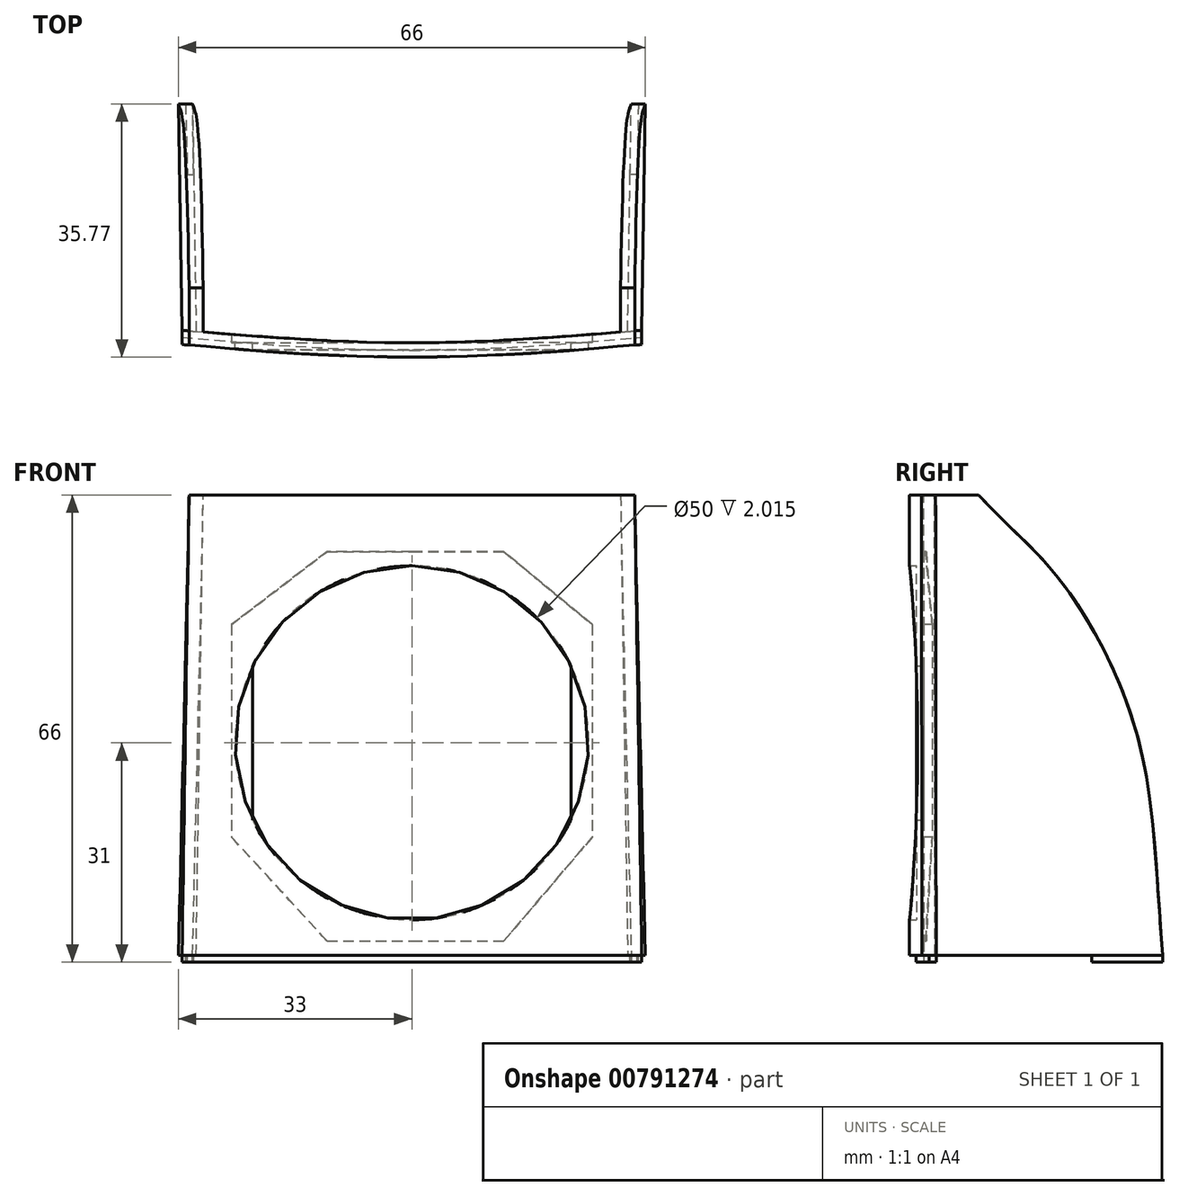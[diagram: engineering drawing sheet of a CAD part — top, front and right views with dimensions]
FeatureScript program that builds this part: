
annotation { "Feature Type Name" : "Feature", "Feature Type Description" : "" }
export const myFeature = defineFeature(function(context is Context, id is Id, definition is map)
    precondition{}
    {
        {
            var Q0;
            Q0=qCreatedBy(makeId("Front.planeOp"),FACE);
            var sketch = newSketch(context, id + "F0", { "sketchPlane" : qUnion([Q0])});
            skLineSegment(sketch, "E0", {"start": v(-32.5, -32.5) * mm, "end": v(32.5, -32.5) * mm});
            skLineSegment(sketch, "E1", {"start": v(32.5, -32.5) * mm, "end": v(31.5, 32.5) * mm});
            skLineSegment(sketch, "E2", {"start": v(31.5, 32.5) * mm, "end": v(-31.5, 32.5) * mm});
            skLineSegment(sketch, "E3", {"start": v(-31.5, 32.5) * mm, "end": v(-32.5, -32.5) * mm});
            skPoint(sketch, "E4", {"position": v(0, -32.5) * mm});
            skPoint(sketch, "E5", {"position": v(0, 32.5) * mm});
            skPoint(sketch, "E6", {"position": v(0, 0) * mm});
            skSolve(sketch);
        }
        {
            var Q0;
            Q0=makeQuery(id+"F0.imprint","IMPRINT",FACE,{"disambiguationData":[TD([[makeQuery(id+"F0.imprint","IMPRINT",EDGE,{"derivedFrom":sQuery(id+"F0.wireOp",EDGE,"E0")}),1.0]])]});
            extrude(context, id + "F1", {"entities" : qUnion([Q0]), "depth" : 5 * mm, "offsetDistance" : 25 * mm});
        }
        {
            var Q0;
            Q0=makeQuery(id+"F1.opExtrude","SWEPT_FACE",FACE,{"disambiguationData":[OSD([sQuery(id+"F0.wireOp",EDGE,"E0")])]});
            var sketch = newSketch(context, id + "F2", { "sketchPlane" : qUnion([Q0])});
            skFitSpline(sketch, "E7", {"points": [v(-32.5, 0) * mm, v(0, 1.76) * mm, v(32.5, 0) * mm], "startDerivative": vector(66, 5.28) * mm, "endDerivative": vector(66, -5.28) * mm});
            skLineSegment(sketch, "E8", {"start": v(-32.5, 0) * mm, "end": v(32.5, 0) * mm});
            skFitSpline(sketch, "E9.0", {"points": [v(-32.66, 2) * mm, v(-27.16, 2.43) * mm, v(-18.99, 3.1) * mm, v(-9.5, 3.58) * mm, v(-4.07, 3.73) * mm, v(0, 3.77) * mm, v(4.07, 3.73) * mm, v(9.5, 3.58) * mm, v(18.99, 3.1) * mm, v(27.16, 2.43) * mm, v(32.66, 2) * mm]});
            skLineSegment(sketch, "E10", {"start": v(32.66, 2) * mm, "end": v(32.5, 5) * mm});
            skLineSegment(sketch, "E11", {"start": v(32.5, 5) * mm, "end": v(-32.5, 5) * mm});
            skLineSegment(sketch, "E12", {"start": v(-32.5, 5) * mm, "end": v(-32.66, 2) * mm});
            skFitSpline(sketch, "E13.0", {"points": [v(-32.58, 1) * mm, v(-27.08, 1.44) * mm, v(-18.91, 2.1) * mm, v(-8.1, 2.65) * mm, v(0, 2.82) * mm, v(8.1, 2.65) * mm, v(18.91, 2.1) * mm, v(27.08, 1.44) * mm, v(32.58, 1) * mm]});
            skLineSegment(sketch, "E14", {"start": v(32.5, 0) * mm, "end": v(32.58, 1) * mm});
            skLineSegment(sketch, "E15", {"start": v(-32.5, 0) * mm, "end": v(-32.58, 1) * mm});
            skSolve(sketch);
        }
        {
            var Q0;
            {var subQ6=sQuery(id+"F2.wireOp",EDGE,"E11");Q0=makeQuery(id+"F2.imprint","IMPRINT",FACE,{"disambiguationData":[TD([[makeQuery(id+"F2.imprint","IMPRINT",EDGE,{"derivedFrom":subQ6}),-1.0]])]});}
            var Q1;
            Q1=makeQuery(id+"F2.imprint","IMPRINT",FACE,{"disambiguationData":[TD([[makeQuery(id+"F2.imprint","IMPRINT",EDGE,{"derivedFrom":sQuery(id+"F2.wireOp",EDGE,"E7")}),-1.0]])]});
            extrude(context, id + "F3", {"entities" : qUnion([Q0, Q1]), "operationType" : NewBodyOperationType.REMOVE, "oppositeDirection" : true, "depth" : 65 * mm, "offsetDistance" : 25 * mm});
        }
        {
            var Q0;
            Q0=qCreatedBy(makeId("Front.planeOp"),FACE);
            var sketch = newSketch(context, id + "F4", { "sketchPlane" : qUnion([Q0])});
            skCircle(sketch, "E16", {"center": v(0, -2.5) * mm, "radius": 25 * mm});
            skPoint(sketch, "E17", {"position": v(0, 22.5) * mm});
            skSolve(sketch);
        }
        {
            var Q0;
            Q0 = qSketchRegion(id + "F4", true);
            extrude(context, id + "F5", {"entities" : qUnion([Q0]), "operationType" : NewBodyOperationType.REMOVE, "depth" : 25 * mm, "offsetDistance" : 25 * mm});
        }
        {
            var Q0;
            Q0=makeQuery(id+"F1.opExtrude","SWEPT_FACE",FACE,{"disambiguationData":[OSD([sQuery(id+"F0.wireOp",EDGE,"E0")])]});
            var sketch = newSketch(context, id + "F6", { "sketchPlane" : qUnion([Q0])});
            skLineSegment(sketch, "E18", {"start": v(-32.5, 0) * mm, "end": v(-33, -32) * mm});
            skLineSegment(sketch, "E19", {"start": v(-33, -32) * mm, "end": v(-31, -32) * mm});
            skLineSegment(sketch, "E20", {"start": v(-31, -32) * mm, "end": v(-30.5, 0.16) * mm});
            skLineSegment(sketch, "E21", {"start": v(-30.5, 0.16) * mm, "end": v(-32.5, 0) * mm});
            skLineSegment(sketch, "E22", {"start": v(32.5, 0) * mm, "end": v(30.5, 0.16) * mm});
            skLineSegment(sketch, "E23", {"start": v(30.5, 0.16) * mm, "end": v(31, -32) * mm});
            skLineSegment(sketch, "E24", {"start": v(31, -32) * mm, "end": v(33, -32) * mm});
            skLineSegment(sketch, "E25", {"start": v(33, -32) * mm, "end": v(32.5, 0) * mm});
            skPoint(sketch, "E26", {"position": v(0, -32) * mm});
            skLineSegment(sketch, "E27", {"start": v(32.5, 0) * mm, "end": v(30.5, 0) * mm, "construction": true});
            skLineSegment(sketch, "E28", {"start": v(-32.5, 0) * mm, "end": v(-30.5, 0) * mm, "construction": true});
            skSolve(sketch);
        }
        {
            var Q0;
            Q0=makeQuery(id+"F1.opExtrude","SWEPT_FACE",FACE,{"disambiguationData":[OSD([sQuery(id+"F0.wireOp",EDGE,"E2")])]});
            var sketch = newSketch(context, id + "F7", { "sketchPlane" : qUnion([Q0])});
            skLineSegment(sketch, "E29", {"start": v(-31.5, -0.08) * mm, "end": v(-29.5, -0.24) * mm});
            skLineSegment(sketch, "E30", {"start": v(-29.5, -0.24) * mm, "end": v(-29.5, 32) * mm});
            skLineSegment(sketch, "E31", {"start": v(-29.5, 32) * mm, "end": v(-31.5, 32) * mm});
            skLineSegment(sketch, "E32", {"start": v(-31.5, 32) * mm, "end": v(-31.5, -0.08) * mm});
            skLineSegment(sketch, "E33", {"start": v(31.5, -0.08) * mm, "end": v(29.5, -0.24) * mm});
            skLineSegment(sketch, "E34", {"start": v(29.5, -0.24) * mm, "end": v(29.5, 32) * mm});
            skLineSegment(sketch, "E35", {"start": v(29.5, 32) * mm, "end": v(31.5, 32) * mm});
            skLineSegment(sketch, "E36", {"start": v(31.5, 32) * mm, "end": v(31.5, -0.08) * mm});
            skLineSegment(sketch, "E37", {"start": v(-31.5, -0.08) * mm, "end": v(-29.5, -0.08) * mm, "construction": true});
            skLineSegment(sketch, "E38", {"start": v(31.5, -0.08) * mm, "end": v(29.5, -0.08) * mm, "construction": true});
            skPoint(sketch, "E39", {"position": v(0, 32) * mm});
            skSolve(sketch);
        }
        {
            var Q1;
            Q1=makeQuery(id+"F6.imprint","IMPRINT",FACE,{"disambiguationData":[TD([[makeQuery(id+"F6.imprint","IMPRINT",EDGE,{"derivedFrom":sQuery(id+"F6.wireOp",EDGE,"E18")}),1.0]])]});
            var Q2;
            Q2=makeQuery(id+"F7.imprint","IMPRINT",FACE,{"disambiguationData":[TD([[makeQuery(id+"F7.imprint","IMPRINT",EDGE,{"derivedFrom":sQuery(id+"F7.wireOp",EDGE,"E29")}),1.0]])]});
            loft(context, id + "F8", {"operationType" : NewBodyOperationType.ADD, "sheetProfilesArray" : [{ "sheetProfileEntities" : qUnion([Q1]) }, { "sheetProfileEntities" : qUnion([Q2]) }]});
        }
        {
            var Q1;
            Q1=makeQuery(id+"F7.imprint","IMPRINT",FACE,{"disambiguationData":[TD([[makeQuery(id+"F7.imprint","IMPRINT",EDGE,{"derivedFrom":sQuery(id+"F7.wireOp",EDGE,"E33")}),1.0]])]});
            var Q2;
            Q2=makeQuery(id+"F6.imprint","IMPRINT",FACE,{"disambiguationData":[TD([[makeQuery(id+"F6.imprint","IMPRINT",EDGE,{"derivedFrom":sQuery(id+"F6.wireOp",EDGE,"E22")}),-1.0]])]});
            loft(context, id + "F9", {"operationType" : NewBodyOperationType.ADD, "sheetProfilesArray" : [{ "sheetProfileEntities" : qUnion([Q1]) }, { "sheetProfileEntities" : qUnion([Q2]) }]});
        }
        {
            var Q0;
            Q0=qCreatedBy(makeId("Right.planeOp"),FACE);
            var sketch = newSketch(context, id + "F10", { "sketchPlane" : qUnion([Q0])});
            skLineSegment(sketch, "E40", {"start": v(0, 32.5) * mm, "end": v(6, 32.5) * mm});
            skLineSegment(sketch, "E41", {"start": v(32, -32.5) * mm, "end": v(0, -32.5) * mm});
            skLineSegment(sketch, "E42", {"start": v(0, -32.5) * mm, "end": v(0, 32.5) * mm});
            skLineSegment(sketch, "E43", {"start": v(32, -32.5) * mm, "end": v(32, 32.5) * mm});
            skPoint(sketch, "E43.endSnap0", {"position": v(3, 32.5) * mm});
            skLineSegment(sketch, "E44", {"start": v(32, 32.5) * mm, "end": v(6, 32.5) * mm});
            skPoint(sketch, "E45", {"position": v(28, 0) * mm});
            skFitSpline(sketch, "E46", {"points": [v(6, 32.5) * mm, v(17, 21.1) * mm, v(28, 0) * mm, v(31, -18.45) * mm, v(32, -32.5) * mm], "startDerivative": vector(39.95, -44.58) * mm, "endDerivative": vector(5.9, -79.66) * mm});
            skSolve(sketch);
        }
        {
            var Q0;
            Q0=makeQuery(id+"F10.imprint","IMPRINT",FACE,{"disambiguationData":[TD([[makeQuery(id+"F10.imprint","IMPRINT",EDGE,{"derivedFrom":sQuery(id+"F10.wireOp",EDGE,"E43")}),1.0]])]});
            extrude(context, id + "F11", {"entities" : qUnion([Q0]), "operationType" : NewBodyOperationType.REMOVE, "endBound" : BoundingType.SYMMETRIC, "depth" : 70 * mm, "offsetDistance" : 25 * mm});
        }
        {
            var Q0;
            {var subQ0=sQuery(id+"F2.wireOp",EDGE,"E7");Q0=makeQuery(id+"F2.imprint","IMPRINT",FACE,{"disambiguationData":[TD([[makeQuery(id+"F2.imprint","IMPRINT",EDGE,{"derivedFrom":subQ0}),1.0]])]});}
            extrude(context, id + "F12", {"entities" : qUnion([Q0]), "operationType" : NewBodyOperationType.ADD, "depth" : 1 * mm, "offsetDistance" : 25 * mm});
        }
        {
            var Q0;
            Q0=makeQuery(id+"F6.imprint","IMPRINT",FACE,{"disambiguationData":[TD([[makeQuery(id+"F6.imprint","IMPRINT",EDGE,{"derivedFrom":sQuery(id+"F6.wireOp",EDGE,"E22")}),-1.0]])]});
            var sketch = newSketch(context, id + "F13", { "sketchPlane" : qUnion([Q0])});
            skLineSegment(sketch, "E47", {"start": v(31, -32) * mm, "end": v(32, -32) * mm});
            skLineSegment(sketch, "E48", {"start": v(32, -32) * mm, "end": v(31.85, -22) * mm});
            skLineSegment(sketch, "E49", {"start": v(31.85, -22) * mm, "end": v(30.85, -22) * mm});
            skLineSegment(sketch, "E50", {"start": v(30.85, -22) * mm, "end": v(31, -32) * mm});
            skLineSegment(sketch, "E51", {"start": v(-31, -32) * mm, "end": v(-32, -32) * mm});
            skLineSegment(sketch, "E52", {"start": v(-32, -32) * mm, "end": v(-31.73, -22) * mm});
            skLineSegment(sketch, "E53", {"start": v(-31.73, -22) * mm, "end": v(-30.85, -22) * mm});
            skLineSegment(sketch, "E54", {"start": v(-30.85, -22) * mm, "end": v(-31, -32) * mm});
            skSolve(sketch);
        }
        {
            var Q0;
            Q0 = qSketchRegion(id + "F13", true);
            extrude(context, id + "F14", {"entities" : qUnion([Q0]), "operationType" : NewBodyOperationType.ADD, "depth" : 1 * mm, "offsetDistance" : 25 * mm});
        }
        {
            var Q0;
            {var subQ1=sQuery(id+"F6.wireOp",EDGE,"E21");Q0=makeQuery(id+"F6.imprint","IMPRINT",FACE,{"disambiguationData":[TD([[makeQuery(id+"F6.imprint","IMPRINT",EDGE,{"derivedFrom":subQ1}),1.0]])]});}
            var sketch = newSketch(context, id + "F15", { "sketchPlane" : qUnion([Q0])});
            skLineSegment(sketch, "E55.bottom", {"start": v(-22.5, 1.76) * mm, "end": v(22.5, 1.76) * mm});
            skLineSegment(sketch, "E55.top", {"start": v(-22.5, 2.76) * mm, "end": v(22.5, 2.76) * mm});
            skLineSegment(sketch, "E55.left", {"start": v(-22.5, 1.76) * mm, "end": v(-22.5, 2.76) * mm});
            skLineSegment(sketch, "E55.right", {"start": v(22.5, 1.76) * mm, "end": v(22.5, 2.76) * mm});
            skPoint(sketch, "E55.middle", {"position": v(0, 2.26) * mm});
            skSolve(sketch);
        }
        {
            var Q0;
            Q0 = qSketchRegion(id + "F15", true);
            extrude(context, id + "F16", {"entities" : qUnion([Q0]), "operationType" : NewBodyOperationType.ADD, "oppositeDirection" : true, "depth" : 57.3 * mm, "offsetDistance" : 25 * mm});
        }
        {
            var Q0;
            Q0=makeQuery(id+"F16.opExtrude","SWEPT_FACE",FACE,{"disambiguationData":[OSD([sQuery(id+"F15.wireOp",EDGE,"E55.bottom")])]});
            var sketch = newSketch(context, id + "F17", { "sketchPlane" : qUnion([Q0])});
            skLineSegment(sketch, "E56", {"start": v(-13, 24.5) * mm, "end": v(12, 24.5) * mm});
            skLineSegment(sketch, "E57", {"start": v(12, 24.5) * mm, "end": v(25.5, 14.18) * mm});
            skLineSegment(sketch, "E58", {"start": v(25.5, 14.18) * mm, "end": v(25.5, -15.82) * mm});
            skLineSegment(sketch, "E59", {"start": v(25.5, -15.82) * mm, "end": v(12, -30.5) * mm});
            skLineSegment(sketch, "E60", {"start": v(12, -30.5) * mm, "end": v(-13, -30.5) * mm});
            skLineSegment(sketch, "E61", {"start": v(-13, -30.5) * mm, "end": v(-25.5, -15.82) * mm});
            skLineSegment(sketch, "E62", {"start": v(-25.5, -15.82) * mm, "end": v(-25.5, 14.18) * mm});
            skLineSegment(sketch, "E63", {"start": v(-25.5, 14.18) * mm, "end": v(-13, 24.5) * mm});
            skPoint(sketch, "E64", {"position": v(25.5, -0.82) * mm});
            skPoint(sketch, "E65", {"position": v(-25.5, -0.82) * mm});
            skPoint(sketch, "E66", {"position": v(-0.5, 24.5) * mm});
            skPoint(sketch, "E67", {"position": v(-0.5, -30.5) * mm});
            skLineSegment(sketch, "E68", {"start": v(-0.5, -30.5) * mm, "end": v(-0.5, 24.5) * mm, "construction": true});
            skSolve(sketch);
        }
        {
            var Q0;
            Q0 = qSketchRegion(id + "F17", true);
            extrude(context, id + "F18", {"entities" : qUnion([Q0]), "operationType" : NewBodyOperationType.REMOVE, "depth" : 25 * mm, "offsetDistance" : 25 * mm});
        }
    });
